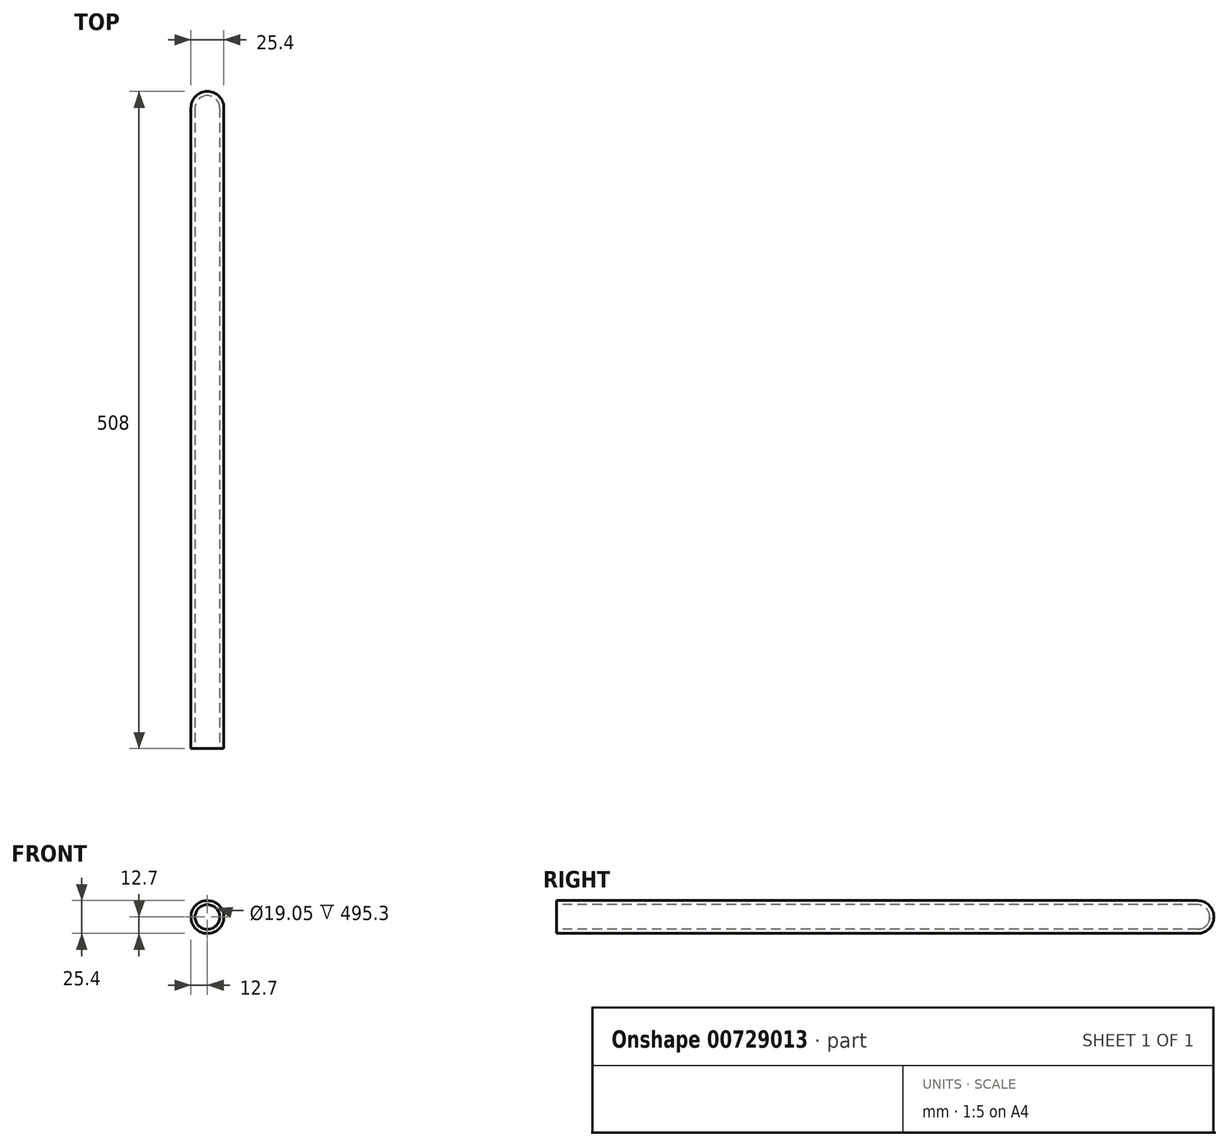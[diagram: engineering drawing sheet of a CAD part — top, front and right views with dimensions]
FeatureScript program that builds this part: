
annotation { "Feature Type Name" : "Feature", "Feature Type Description" : "" }
export const myFeature = defineFeature(function(context is Context, id is Id, definition is map)
    precondition{}
    {
        {
            var Q0;
            Q0=qCreatedBy(makeId("Front.planeOp"),FACE);
            var sketch = newSketch(context, id + "F0", { "sketchPlane" : qUnion([Q0])});
            skCircle(sketch, "E0", {"center": v(0, 0) * mm, "radius": 12.7 * mm});
            skSolve(sketch);
        }
        {
            var Q0;
            Q0 = qSketchRegion(id + "F0", true);
            extrude(context, id + "F1", {"entities" : qUnion([Q0]), "oppositeDirection" : true, "depth" : 508 * mm, "offsetDistance" : 25.4 * mm});
        }
        {
            var Q0;
            Q0=makeQuery(id+"F1.opExtrude","CAP_FACE",FACE,{"disambiguationData":[OSD([sQuery(id+"F0.wireOp",EDGE,"E0")])],"isStart":false});
            fillet(context, id + "F2", {"entities" : qUnion([Q0]), "radius" : 12.7 * mm, "tangentPropagation" : true, "allowEdgeOverflow" : false});
        }
        {
            var Q0;
            Q0=makeQuery(id+"F1.opExtrude","CAP_FACE",FACE,{"disambiguationData":[OSD([sQuery(id+"F0.wireOp",EDGE,"E0")])],"isStart":true});
            shell(context, id + "F3", {"entities" : qUnion([Q0]), "thickness" : 3.17 * mm});
        }
    });
